# Revit family: Maxlogic sounder,becaon, sounder & becaon (High IP)
name_source: partatom
category: Fire Alarm Devices
units: mm (PartAtom-declared; Revit-internal decimal feet)

## family parameters
Cut with Voids When Loaded = No
Host = Face
Maintain Annotation Orientation = Yes
OmniClass Number = 23.85.30.21
OmniClass Title = Environmental Detection/Registration
Part Type = Normal
Room Calculation Point = No
Round Connector Dimension = Use Diameter
Shared = No

## types (24) — shared parameters
Color = Red
Fax Number = (+)90 216 466 45 10
Installation Manual = https://mavilielektronik.com
Main Material = Red Plastic PC/ABS
Manufacturer = Mavili Elektronik Ticaret A.Ş.
Model = Maxlogic
Mounting height = 240 cm above from ground
Mounting surface = Wall mounting
Nominal Height = 95 mm
Nominal Width = 95 mm
Operating temperature = (-25°C) - (+70°C)
Operatonal Voltage (default) = 24 V/DC
Secondary Material = Plastic
URL = https://www.mavili.com.tr
Warranty Duration Labor = 2
Warranty Duration Parts = 2
Warranty Duration Unit = Year
zero-valued in all types: Cost, Default Elevation

## per-type parameters (varying)
| type | Beacon | Beacon,Sounder Beacon Ceiling | Code Performance | Description | Device Adress Setup | IP 33 Mounting Box | IP 65 Mounting Box | Nominal Depth | Operating voltage range | Product Code | Protection Sign | Sounder Ceiling | Weight |
| Maxlogic Conventional Sounder, Weatherproof (IP33) | No | No | EN 54-3 | Conventional Sounder, Weatherproof |  | Yes | No | 82 mm | 21-28V/DC | ML-2440 | IP 33 | Yes | 154 |
| Maxlogic Conventional Beacon, Weatherproof (IP33) | Yes | Yes | EN 54-23 | Conventional Beacon, Weatherproof |  | Yes | No | 82 mm | 21-28V/DC | ML-2450 | IP 33 | No | 149 gr |
| Maxlogic Conventional Sounder & Beacon, Weatherproof (IP33) | Yes | Yes | EN 54-3 / EN 54-23 | Conventional Sounder & Beacon, Weatherproof |  | Yes | No | 82 mm | 21-28V/DC | ML-2460 | IP 33 | No | 166 gr |
| Maxlogic Conventional Sounder, Weatherproof (IP65) | No | No | EN 54-3 | Conventional Sounder, Weatherproof |  | No | Yes | 100 mm | 21-28V/DC | ML-2470 | IP 65 | Yes | 173 gr |
| Maxlogic Conventional Beacon, Weatherproof (IP65) | Yes | Yes | EN 54-23 | Conventional Beacon, Weatherproof |  | No | Yes | 107 mm | 21-28V/DC | ML-2480 | IP 65 | No | 168 gr |
| Maxlogic Conventional Sounder & Beacon, Weatherproof (IP65) | Yes | Yes | EN 54-3 / EN 54-23 | Conventional Sounder & Beacon, Weatherproof |  | No | Yes | 107 mm | 21-28V/DC | ML-2490 | IP 65 | No | 185 gr |
| Maxlogic Intelligent Addressable System Sounder, Weatherproof (IP33) | No | No | EN 54-3 | Intelligent Addressable System Sounder, Weatherproof | The address is given to devices by addressable programmer | Yes | No | 82 mm | 18-33V/DC | ML-1440 | IP 33 | Yes | 159 gr |
| Maxlogic Intelligent Addressable System Sounder, Weatherproof (IP33), Short Circuit Isolator | No | No | EN 54-3 | Intelligent Addressable System Sounder, Weatherproof, Short Circuit Isolator | The address is given to devices by addressable programmer | Yes | No | 82 mm | 18-33V/DC | ML-1440.SCI | IP 33 | Yes | 159 gr |
| Maxlogic Intelligent Addressable System Beacon, Weatherproof (IP33) | Yes | Yes | EN 54-23 | Intelligent Addressable System Beacon, Weatherproof | The address is given to devices by addressable programmer | Yes | No | 82 mm | 18-33V/DC | ML-1450 | IP 33 | No | 153 gr |
| Maxlogic Intelligent Addressable System Beacon, Weatherproof (IP33), Short Circuit Isolator | Yes | Yes | EN 54-23 | Intelligent Addressable System Beacon, Weatherproof, Short Circuit Isolator | The address is given to devices by addressable programmer | Yes | No | 82 mm | 18-33V/DC | ML-1450.SCI | IP 33 | No | 153 gr |
| Maxlogic Intelligent Addressable System Sounder & Beacon, Weatherproof (IP33) | Yes | Yes | EN 54-3 / EN 54-23 | Intelligent Addressable System Sounder & Beacon, Weatherproof | The address is given to devices by addressable programmer | Yes | No | 82 mm | 18-33V/DC | ML-1460 | IP 33 | No | 169 gr |
| Maxlogic Intelligent Addressable System Sounder & Beacon, Weatherproof (IP33), Short Circuit Isolator | Yes | Yes | EN 54-3 / EN 54-23 | Intelligent Addressable System Sounder & Beacon, Weatherproof, Short Circuit Isolator | The address is given to devices by addressable programmer | Yes | No | 82 mm | 18-33V/DC | ML-1460.SCI | IP 33 | No | 169 gr |
| Maxlogic Intelligent Addressable System Sounder, Weatherproof (IP65) | No | No | EN 54-3 | Intelligent Addressable System Sounder, Weatherproof | The address is given to devices by addressable programmer | No | Yes | 82 mm | 18-33V/DC | ML-1470 | IP 65 | Yes | 178 gr |
| Maxlogic Intelligent Addressable System Sounder, Weatherproof (IP65), Short Circuit Isolator | No | No | EN 54-3 | Intelligent Addressable System Sounder, Weatherproof, Short Circuit Isolator | The address is given to devices by addressable programmer | No | Yes | 82 mm | 18-33V/DC | ML-1470.SCI | IP 65 | Yes | 178 gr |
| Maxlogic Intelligent Addressable System Beacon, Weatherproof (IP65) | Yes | Yes | EN 54-23 | Intelligent Addressable System Beacon, Weatherproof | The address is given to devices by addressable programmer | No | Yes | 82 mm | 18-33V/DC | ML-1480 | IP 65 | No | 172 gr |
| Maxlogic Intelligent Addressable System Beacon, Weatherproof (IP65), Short Circuit Isolator | Yes | Yes | EN 54-23 | Intelligent Addressable System Beacon, Weatherproof, Short Circuit Isolator | The address is given to devices by addressable programmer | No | Yes | 82 mm | 18-33V/DC | ML-1480.SCI | IP 65 | No | 172 gr |
| Maxlogic Intelligent Addressable System Sounder & Beacon, Weatherproof (IP65) | Yes | Yes | EN 54-3 / EN 54-23 | Intelligent Addressable System Sounder & Beacon, Weatherproof | The address is given to devices by addressable programmer | No | Yes | 82 mm | 18-33V/DC | ML-1490 | IP 65 | No | 188 gr |
| Maxlogic Intelligent Addressable System Sounder & Beacon, Weatherproof (IP65), Short Circuit Isolator | Yes | Yes | EN 54-3 / EN 54-23 | Intelligent Addressable System Sounder & Beacon, Weatherproof, Short Circuit Isolator | The address is given to devices by addressable programmer | No | Yes | 82 mm | 18-33V/DC | ML-1490.SCI | IP 65 | No | 188 gr |
| Maxlogic Addressable Wall Mounted (W Class,IP33) Beacon | Yes | Yes | EN 54-23 | Addressable Wall Mounted (W Class,IP33) Beacon | The address is given to devices by addressable programmer | Yes | No | 82 mm | 18-33V/DC | ML-1423 | IP 33 | No | 153 gr |
| Maxlogic Addressable Wall Mounted (W Class,IP33) Beacon with Short Circuit Isolator | Yes | Yes | EN 54-23 | Addressable Wall Mounted (W Class,IP33) Beacon with Short Circuit Isolator | The address is given to devices by addressable programmer | Yes | No | 82 mm | 18-33V/DC | ML-1423.SCI | IP 33 | No | 153 gr |
| Maxlogic Addressable Wall Mounted (W Class, IP65) Beacon | Yes | Yes | EN 54-23 | Addressable Wall Mounted (W Class, IP65) Beacon | The address is given to devices by addressable programmer | No | Yes | 82 mm | 18-33V/DC | ML-1424 | IP 65 | No | 153 gr |
| Maxlogic Addressable Wall Mounted (W Class, IP65) Beacon with Short Circuit Isolator | Yes | Yes | EN 54-23 | Addressable Wall Mounted (W Class, IP65) Beacon with Short Circuit Isolator | The address is given to devices by addressable programmer | No | Yes | 82 mm | 18-33V/DC | ML-1424.SCI | IP 65 | No | 153 gr |
| Maxlogic Conventional Wall Mounted (Class W, IP33) Beacon | Yes | Yes | EN 54-23 | Conventional Wall Mounted (Class W, IP33) Beacon |  | Yes | No | 82 mm | 21-28V/DC | ML-2423 | IP 33 | No | 153 gr |
| Maxlogic Conventional Wall Mounted (W Class, IP65) Beacon | Yes | Yes | EN 54-23 | Conventional Wall Mounted (W Class, IP65) Beacon |  | No | Yes | 107 mm | 21-28V/DC | ML-2424 | IP 65 | No | 153 gr |

## geometry (parser evidence)
native form markers: Sweep x4
no freeform markers — native parametric forms only
